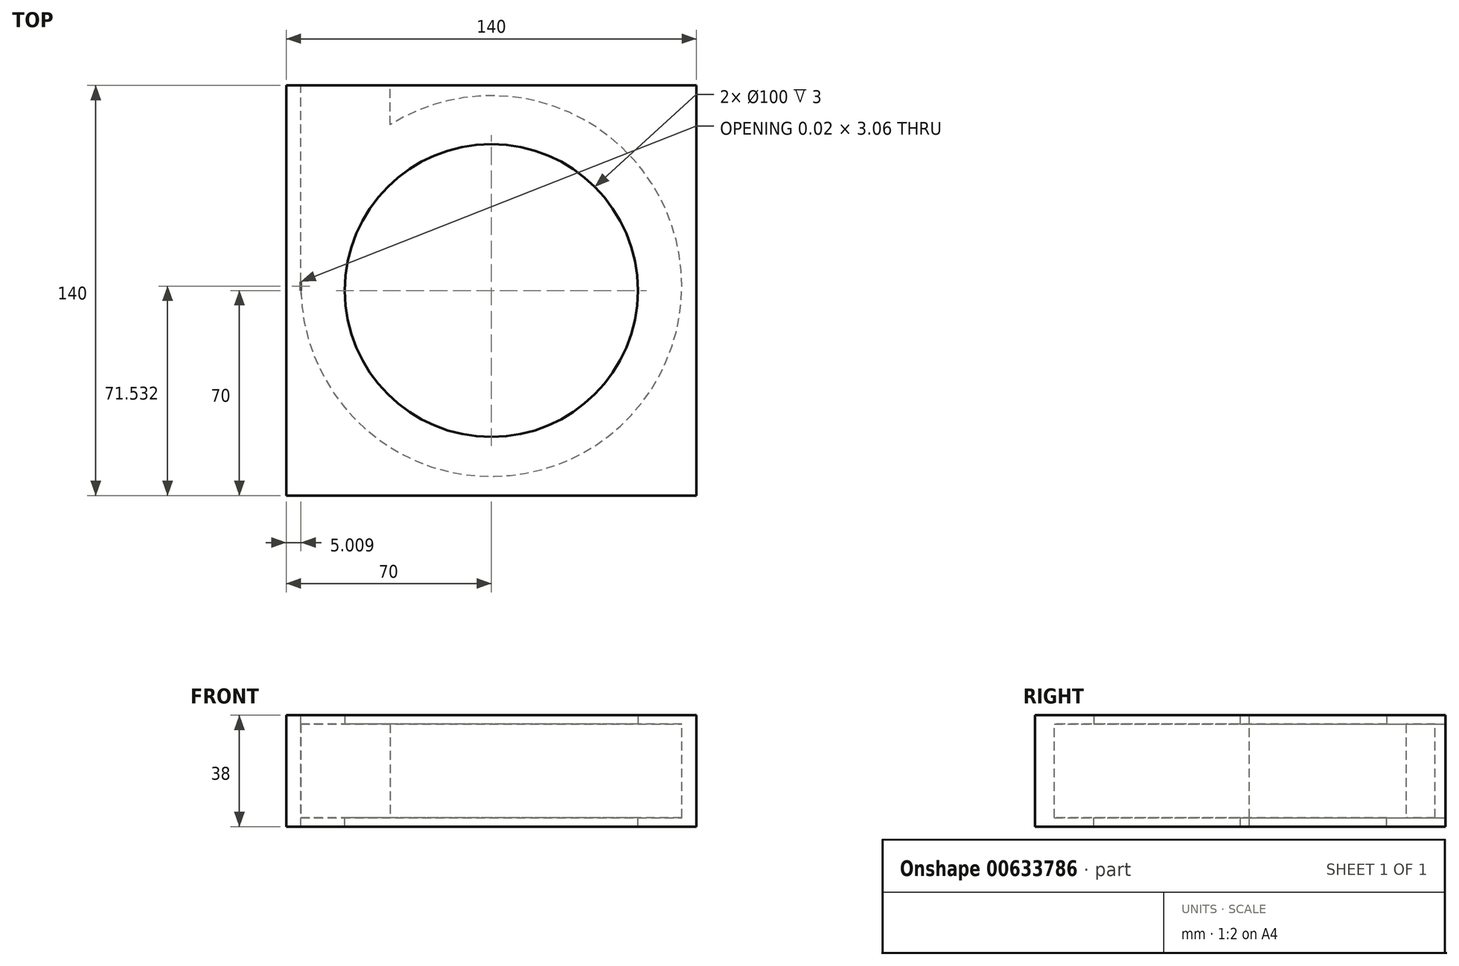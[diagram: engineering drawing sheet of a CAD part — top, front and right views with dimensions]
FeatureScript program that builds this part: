
annotation { "Feature Type Name" : "Feature", "Feature Type Description" : "" }
export const myFeature = defineFeature(function(context is Context, id is Id, definition is map)
    precondition{}
    {
        {
            var Q0;
            Q0=qCreatedBy(makeId("Top.planeOp"),FACE);
            var sketch = newSketch(context, id + "F0", { "sketchPlane" : qUnion([Q0])});
            skCircle(sketch, "E0", {"center": v(0, 0) * mm, "radius": 50 * mm});
            skLineSegment(sketch, "E1.bottom", {"start": v(70, -70) * mm, "end": v(-70, -70) * mm});
            skLineSegment(sketch, "E1.top", {"start": v(70, 70) * mm, "end": v(-70, 70) * mm});
            skLineSegment(sketch, "E1.left", {"start": v(70, -70) * mm, "end": v(70, 70) * mm});
            skLineSegment(sketch, "E1.right", {"start": v(-70, -70) * mm, "end": v(-70, 70) * mm});
            skCircle(sketch, "E2", {"center": v(0, 1.53) * mm, "radius": 65 * mm});
            skLineSegment(sketch, "E3", {"start": v(-34.53, 56.6) * mm, "end": v(-34.53, 70) * mm});
            skLineSegment(sketch, "E4", {"start": v(-64.98, 0) * mm, "end": v(-64.98, 70) * mm});
            skSolve(sketch);
        }
        {
            var Q0;
            Q0=makeQuery(id+"F0.imprint","IMPRINT",FACE,{"disambiguationData":[TD([[makeQuery(id+"F0.imprint","IMPRINT",EDGE,{"derivedFrom":sQuery(id+"F0.wireOp",EDGE,"E1.bottom")}),-1.0]])]});
            var Q1;
            Q1=makeQuery(id+"F0.imprint","IMPRINT",FACE,{"disambiguationData":[TD([[makeQuery(id+"F0.imprint","IMPRINT",EDGE,{"derivedFrom":sQuery(id+"F0.wireOp",EDGE,"E0")}),1.0]])]});
            var Q2;
            {var subQ0=sQuery(id+"F0.wireOp",EDGE,"E3");Q2=makeQuery(id+"F0.imprint","IMPRINT",FACE,{"disambiguationData":[TD([[makeQuery(id+"F0.imprint","IMPRINT",EDGE,{"derivedFrom":subQ0}),1.0]])]});}
            var Q3;
            Q3=makeQuery(id+"F0.imprint","IMPRINT",FACE,{"disambiguationData":[TD([[makeQuery(id+"F0.imprint","IMPRINT",EDGE,{"derivedFrom":sQuery(id+"F0.wireOp",EDGE,"E0")}),-1.0]])]});
            var Q4;
            {var subQ0=sQuery(id+"F0.wireOp",EDGE,"E4");var subQ1=sQuery(id+"F0.wireOp",EDGE,"E2");var subQ2=makeQuery(id+"F0.imprint","INTERSECT",VERTEX,{"disambiguationData":[OD(0.0)],"derivedFrom":[subQ1,subQ0]});Q4=makeQuery(id+"F0.imprint","IMPRINT",FACE,{"disambiguationData":[TD([[makeQuery(id+"F0.imprint","IMPRINT",EDGE,{"disambiguationData":[TD([[subQ2,1.0]])],"derivedFrom":subQ1}),1.0]])]});}
            extrude(context, id + "F1", {"entities" : qUnion([Q0, Q1, Q2, Q3, Q4]), "oppositeDirection" : true, "depth" : 3 * mm, "offsetDistance" : 25 * mm});
        }
        {
            var Q0;
            Q0=makeQuery(id+"F1.opExtrude","CAP_FACE",FACE,{"disambiguationData":[OSD([sQuery(id+"F0.wireOp",EDGE,"E1.bottom"),sQuery(id+"F0.wireOp",EDGE,"E1.top"),sQuery(id+"F0.wireOp",EDGE,"E1.left"),sQuery(id+"F0.wireOp",EDGE,"E1.right")])],"isStart":true});
            extrude(context, id + "F2", {"entities" : qUnion([Q0]), "operationType" : NewBodyOperationType.ADD, "depth" : 35 * mm, "offsetDistance" : 25 * mm});
        }
        {
            var Q0;
            Q0=makeQuery(id+"F0.imprint","IMPRINT",FACE,{"disambiguationData":[TD([[makeQuery(id+"F0.imprint","IMPRINT",EDGE,{"derivedFrom":sQuery(id+"F0.wireOp",EDGE,"E0")}),1.0]])]});
            var Q1;
            Q1=makeQuery(id+"F0.imprint","IMPRINT",FACE,{"disambiguationData":[TD([[makeQuery(id+"F0.imprint","IMPRINT",EDGE,{"derivedFrom":sQuery(id+"F0.wireOp",EDGE,"E0")}),-1.0]])]});
            var Q2;
            {var subQ0=sQuery(id+"F0.wireOp",EDGE,"E3");Q2=makeQuery(id+"F0.imprint","IMPRINT",FACE,{"disambiguationData":[TD([[makeQuery(id+"F0.imprint","IMPRINT",EDGE,{"derivedFrom":subQ0}),1.0]])]});}
            extrude(context, id + "F3", {"entities" : qUnion([Q0, Q1, Q2]), "operationType" : NewBodyOperationType.REMOVE, "depth" : 32 * mm, "offsetDistance" : 25 * mm});
        }
        {
            var Q0;
            Q0=makeQuery(id+"F0.imprint","IMPRINT",FACE,{"disambiguationData":[TD([[makeQuery(id+"F0.imprint","IMPRINT",EDGE,{"derivedFrom":sQuery(id+"F0.wireOp",EDGE,"E0")}),1.0]])]});
            extrude(context, id + "F4", {"entities" : qUnion([Q0]), "operationType" : NewBodyOperationType.REMOVE, "depth" : 84.6 * mm, "offsetDistance" : 25 * mm});
        }
        {
            var Q0;
            Q0=makeQuery(id+"F0.imprint","IMPRINT",FACE,{"disambiguationData":[TD([[makeQuery(id+"F0.imprint","IMPRINT",EDGE,{"derivedFrom":sQuery(id+"F0.wireOp",EDGE,"E0")}),1.0]])]});
            extrude(context, id + "F5", {"entities" : qUnion([Q0]), "operationType" : NewBodyOperationType.REMOVE, "oppositeDirection" : true, "depth" : 25 * mm, "offsetDistance" : 25 * mm});
        }
    });
